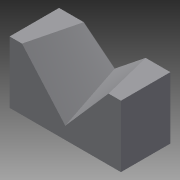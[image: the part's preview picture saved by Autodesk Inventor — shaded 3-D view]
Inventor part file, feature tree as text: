
AUTODESK INVENTOR PART (.ipt)
format: ipt  version: 2015 (Build 190159000, 159)  size: 104,448 bytes
history: native  units: in
note: dims shown in document units (in); Inventor stores cm internally (conversion verified against a paired STEP export)
features: sketch x3, extrude x1, loft x1
ambient origin geometry x8: Origin, YZ Plane, XZ Plane, XY Plane, X Axis, Y Axis, Z Axis, Center Point
bodies: Solid1 (feature_tree)
feature tree (5):
  extrude  "Extrusion1"  Depth=0.3937in
  loft  "Loft1"
  sketch  "Sketch1"  dims[d2=1.5748in d3=0.0in d14=0.3937in]
  sketch  "Sketch4"  dims[d15=0.3937in d16=0.3937in]
  sketch  "Sketch5"  dims[d17=1.7715in d18=0.7874in d19=0.7874in d20=1.1811in d21=1.7715in d22=0.0in d23=90.0deg d24=0.0in d25=90.0deg]
